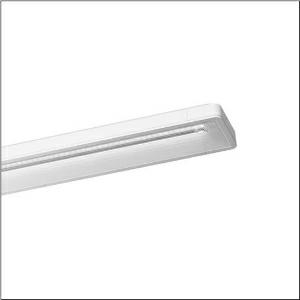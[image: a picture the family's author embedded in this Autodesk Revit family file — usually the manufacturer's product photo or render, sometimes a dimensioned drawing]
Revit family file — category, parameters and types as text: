
# Revit family: taris_r__21_5mt217d03wd_22b7
name_source: partatom
category: Lighting Fixtures
units: mm (PartAtom-declared; Revit-internal decimal feet)

## family parameters
Cut with Voids When Loaded = No
Host = Face
Light Source = No
Part Type = Normal
Room Calculation Point = No
Round Connector Dimension = Use Diameter
Shared = No

## types (1)
- --- (1 x LED, 5700 lm, 35.9 W, 3000K)
    Apparent Load = 36 VA
    CIE Flux Codes = 73 96 99 100 100
    Color Rendering = 80
    Color Temperature = 3000K
    Default Elevation = 1800 mm
    Description = Taris® 21, office luminaire, primary anti-glare with micro louvre, primary optical cover: axial lens, of PMMA, structured, CAT 2 (L<= 1500cd/m²), light emission: direct distribution, primary light characteristic: symmetric, installation type: surface-mounted, LED rated luminous flux: 5.700 lm, light colour: 830, colour temperature: 3000K, control gear: ECG DALI, with terminal, 5-pole, mains connection: 230V, AC, 50Hz, rated input power: 36W, housing, luminaire housing, of plastic, traffic white (RAL 9016), length: 1.510 mm, width: 134 mm, height: 50mm, protection rating (complete): IP20, insulation class (complete): insulation class I (protective earthing), certification: CE, ENEC, VDE, protection symbol: F, impact resistance: IK02, permissible ambient temperature for indoor applications: 0..+35°C, standard: EN 50419, packaging unit: 1 piece
    Height = 51 mm
    Lamp = 1 x LED
    Lamp Light Flux = 5700 lm
    Lamp Power = 35.9 W
    Lamp count = 1
    Length = 1514 mm
    Luminous efficacy = 159 lm/W
    Manufacturer = Siteco
    ModVariant = No
    Model = 5MT217D03WD
    Mounting Place = Ceiling
    Mounting Type = Surface mounted
    Number of Poles = 1
    OnlyDefault = Yes
    Power Factor = 1
    Product Name = Taris® 21
    Product group = office luminaire | ceiling mounted
    ProductGroupID = 302
    Protection Class = Protection class I
    Protection Degree = IP 20
    RLX_Detail_Level = 1
    RlxData = <blob elided: 42525 chars, md5=cd867e7f>
    Socket = socket
    Standby Power = 0 W
    System Light Flux = 5700 lm
    System Power = 36 W
    Type Comments = factory setting: luminous flux: 100 % | dim-lin: 254 | 200 mA
    Type Image = l_1004728.jpg
    URL = http://relux.com
    VarID = @adj_130319
    Voltage = 0 V
    Weight = 0.00 kg
    Width = 134 mm

## geometry (parser evidence)
native form markers: Blend x4, Sweep x11
no freeform markers — native parametric forms only
